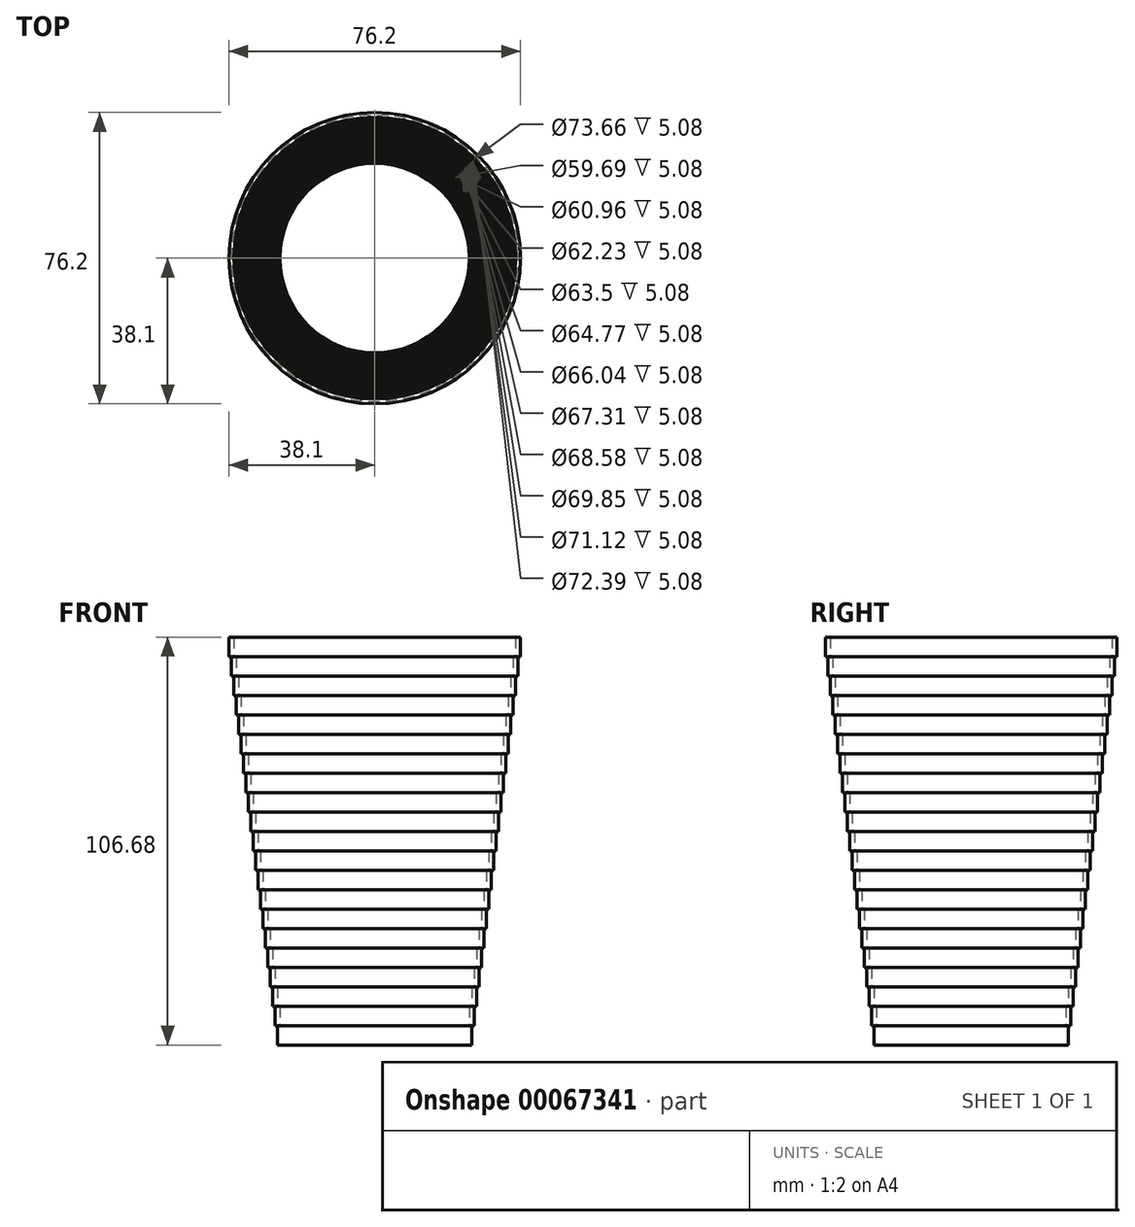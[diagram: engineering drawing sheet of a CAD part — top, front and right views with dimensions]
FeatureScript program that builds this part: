
annotation { "Feature Type Name" : "Feature", "Feature Type Description" : "" }
export const myFeature = defineFeature(function(context is Context, id is Id, definition is map)
    precondition{}
    {
        {
            var Q0;
            Q0=qCreatedBy(makeId("Top.planeOp"),FACE);
            var sketch = newSketch(context, id + "F0", { "sketchPlane" : qUnion([Q0])});
            skCircle(sketch, "E0", {"center": v(0, 0) * mm, "radius": 25.4 * mm});
            skSolve(sketch);
        }
        {
            var Q0;
            Q0=makeQuery(id+"F0.imprint","IMPRINT",FACE,{"disambiguationData":[TD([[makeQuery(id+"F0.imprint","IMPRINT",EDGE,{"derivedFrom":sQuery(id+"F0.wireOp",EDGE,"E0")}),1.0]])]});
            extrude(context, id + "F1", {"entities" : qUnion([Q0]), "depth" : 5.08 * mm});
        }
        {
            var Q0;
            Q0=makeQuery(id+"F1.opExtrude","CAP_FACE",FACE,{"disambiguationData":[OSD([sQuery(id+"F0.wireOp",EDGE,"E0")])],"isStart":false});
            var sketch = newSketch(context, id + "F2", { "sketchPlane" : qUnion([Q0])});
            skCircle(sketch, "E1", {"center": v(0, 0) * mm, "radius": 26.04 * mm});
            skCircle(sketch, "E2", {"center": v(0, 0) * mm, "radius": 24.77 * mm});
            skSolve(sketch);
        }
        {
            var Q0;
            Q0=makeQuery(id+"F2.imprint","IMPRINT",FACE,{"disambiguationData":[TD([[makeQuery(id+"F2.imprint","IMPRINT",EDGE,{"derivedFrom":sQuery(id+"F2.wireOp",EDGE,"E1")}),1.0]])]});
            var Q1;
            Q1=makeQuery(id+"F2.imprint","IMPRINT",FACE,{"disambiguationData":[TD([[makeQuery(id+"F2.imprint","IMPRINT",EDGE,{"derivedFrom":sQuery(id+"F2.wireOp",EDGE,"E2")}),-1.0]])]});
            extrude(context, id + "F3", {"entities" : qUnion([Q0, Q1]), "operationType" : NewBodyOperationType.ADD, "depth" : 5.08 * mm});
        }
        {
            var Q0;
            Q0=makeQuery(id+"F3.opExtrude","CAP_FACE",FACE,{"disambiguationData":[OSD([sQuery(id+"F2.wireOp",EDGE,"E1"),sQuery(id+"F2.wireOp",EDGE,"E2")])],"isStart":false});
            var sketch = newSketch(context, id + "F4", { "sketchPlane" : qUnion([Q0])});
            skCircle(sketch, "E3", {"center": v(0, 0) * mm, "radius": 26.67 * mm});
            skCircle(sketch, "E4", {"center": v(0, 0) * mm, "radius": 25.4 * mm});
            skSolve(sketch);
        }
        {
            var Q0;
            Q0=makeQuery(id+"F4.imprint","IMPRINT",FACE,{"disambiguationData":[TD([[makeQuery(id+"F4.imprint","IMPRINT",EDGE,{"derivedFrom":sQuery(id+"F4.wireOp",EDGE,"E4")}),-1.0]])]});
            var Q1;
            Q1=makeQuery(id+"F4.imprint","IMPRINT",FACE,{"disambiguationData":[TD([[makeQuery(id+"F4.imprint","IMPRINT",EDGE,{"derivedFrom":sQuery(id+"F4.wireOp",EDGE,"E3")}),1.0]])]});
            extrude(context, id + "F5", {"entities" : qUnion([Q0, Q1]), "operationType" : NewBodyOperationType.ADD, "depth" : 5.08 * mm});
        }
        {
            var Q0;
            Q0=makeQuery(id+"F5.opExtrude","CAP_FACE",FACE,{"disambiguationData":[OSD([sQuery(id+"F4.wireOp",EDGE,"E3"),sQuery(id+"F4.wireOp",EDGE,"E4")])],"isStart":false});
            var sketch = newSketch(context, id + "F6", { "sketchPlane" : qUnion([Q0])});
            skCircle(sketch, "E5", {"center": v(0, 0) * mm, "radius": 27.3 * mm});
            skCircle(sketch, "E6", {"center": v(0, 0) * mm, "radius": 26.04 * mm});
            skSolve(sketch);
        }
        {
            var Q0;
            Q0=makeQuery(id+"F6.imprint","IMPRINT",FACE,{"disambiguationData":[TD([[makeQuery(id+"F6.imprint","IMPRINT",EDGE,{"derivedFrom":sQuery(id+"F6.wireOp",EDGE,"E5")}),1.0]])]});
            var Q1;
            Q1=makeQuery(id+"F6.imprint","IMPRINT",FACE,{"disambiguationData":[TD([[makeQuery(id+"F6.imprint","IMPRINT",EDGE,{"derivedFrom":sQuery(id+"F6.wireOp",EDGE,"E6")}),-1.0]])]});
            extrude(context, id + "F7", {"entities" : qUnion([Q0, Q1]), "operationType" : NewBodyOperationType.ADD, "depth" : 5.08 * mm});
        }
        {
            var Q0;
            Q0=makeQuery(id+"F7.opExtrude","CAP_FACE",FACE,{"disambiguationData":[OSD([sQuery(id+"F6.wireOp",EDGE,"E5"),sQuery(id+"F6.wireOp",EDGE,"E6")])],"isStart":false});
            var sketch = newSketch(context, id + "F8", { "sketchPlane" : qUnion([Q0])});
            skCircle(sketch, "E7", {"center": v(0, 0) * mm, "radius": 27.94 * mm});
            skCircle(sketch, "E8", {"center": v(0, 0) * mm, "radius": 26.67 * mm});
            skSolve(sketch);
        }
        {
            var Q0;
            Q0=makeQuery(id+"F8.imprint","IMPRINT",FACE,{"disambiguationData":[TD([[makeQuery(id+"F8.imprint","IMPRINT",EDGE,{"derivedFrom":sQuery(id+"F8.wireOp",EDGE,"E8")}),-1.0]])]});
            var Q1;
            Q1=makeQuery(id+"F8.imprint","IMPRINT",FACE,{"disambiguationData":[TD([[makeQuery(id+"F8.imprint","IMPRINT",EDGE,{"derivedFrom":sQuery(id+"F8.wireOp",EDGE,"E7")}),1.0]])]});
            extrude(context, id + "F9", {"entities" : qUnion([Q0, Q1]), "operationType" : NewBodyOperationType.ADD, "depth" : 5.08 * mm});
        }
        {
            var Q0;
            Q0=makeQuery(id+"F9.opExtrude","CAP_FACE",FACE,{"disambiguationData":[OSD([sQuery(id+"F8.wireOp",EDGE,"E7"),sQuery(id+"F8.wireOp",EDGE,"E8")])],"isStart":false});
            var sketch = newSketch(context, id + "F10", { "sketchPlane" : qUnion([Q0])});
            skCircle(sketch, "E9", {"center": v(0, 0) * mm, "radius": 28.58 * mm});
            skCircle(sketch, "E10", {"center": v(0, 0) * mm, "radius": 27.3 * mm});
            skSolve(sketch);
        }
        {
            var Q0;
            Q0=makeQuery(id+"F10.imprint","IMPRINT",FACE,{"disambiguationData":[TD([[makeQuery(id+"F10.imprint","IMPRINT",EDGE,{"derivedFrom":sQuery(id+"F10.wireOp",EDGE,"E9")}),1.0]])]});
            var Q1;
            Q1=makeQuery(id+"F10.imprint","IMPRINT",FACE,{"disambiguationData":[TD([[makeQuery(id+"F10.imprint","IMPRINT",EDGE,{"derivedFrom":sQuery(id+"F10.wireOp",EDGE,"E10")}),-1.0]])]});
            extrude(context, id + "F11", {"entities" : qUnion([Q0, Q1]), "operationType" : NewBodyOperationType.ADD, "depth" : 5.08 * mm});
        }
        {
            var Q0;
            Q0=makeQuery(id+"F11.opExtrude","CAP_FACE",FACE,{"disambiguationData":[OSD([sQuery(id+"F10.wireOp",EDGE,"E9"),sQuery(id+"F10.wireOp",EDGE,"E10")])],"isStart":false});
            var sketch = newSketch(context, id + "F12", { "sketchPlane" : qUnion([Q0])});
            skCircle(sketch, "E11", {"center": v(0, 0) * mm, "radius": 29.21 * mm});
            skCircle(sketch, "E12", {"center": v(0, 0) * mm, "radius": 27.94 * mm});
            skSolve(sketch);
        }
        {
            var Q0;
            Q0=makeQuery(id+"F12.imprint","IMPRINT",FACE,{"disambiguationData":[TD([[makeQuery(id+"F12.imprint","IMPRINT",EDGE,{"derivedFrom":sQuery(id+"F12.wireOp",EDGE,"E12")}),-1.0]])]});
            var Q1;
            Q1=makeQuery(id+"F12.imprint","IMPRINT",FACE,{"disambiguationData":[TD([[makeQuery(id+"F12.imprint","IMPRINT",EDGE,{"derivedFrom":sQuery(id+"F12.wireOp",EDGE,"E11")}),1.0]])]});
            extrude(context, id + "F13", {"entities" : qUnion([Q0, Q1]), "operationType" : NewBodyOperationType.ADD, "depth" : 5.08 * mm});
        }
        {
            var Q0;
            Q0=makeQuery(id+"F13.opExtrude","CAP_FACE",FACE,{"disambiguationData":[OSD([sQuery(id+"F12.wireOp",EDGE,"E11"),sQuery(id+"F12.wireOp",EDGE,"E12")])],"isStart":false});
            var sketch = newSketch(context, id + "F14", { "sketchPlane" : qUnion([Q0])});
            skCircle(sketch, "E13", {"center": v(0, 0) * mm, "radius": 29.85 * mm});
            skCircle(sketch, "E14", {"center": v(0, 0) * mm, "radius": 28.58 * mm});
            skSolve(sketch);
        }
        {
            var Q0;
            Q0=makeQuery(id+"F14.imprint","IMPRINT",FACE,{"disambiguationData":[TD([[makeQuery(id+"F14.imprint","IMPRINT",EDGE,{"derivedFrom":sQuery(id+"F14.wireOp",EDGE,"E13")}),1.0]])]});
            var Q1;
            Q1=makeQuery(id+"F14.imprint","IMPRINT",FACE,{"disambiguationData":[TD([[makeQuery(id+"F14.imprint","IMPRINT",EDGE,{"derivedFrom":sQuery(id+"F14.wireOp",EDGE,"E14")}),-1.0]])]});
            extrude(context, id + "F15", {"entities" : qUnion([Q0, Q1]), "operationType" : NewBodyOperationType.ADD, "depth" : 5.08 * mm});
        }
        {
            var Q0;
            Q0=makeQuery(id+"F15.opExtrude","CAP_FACE",FACE,{"disambiguationData":[OSD([sQuery(id+"F14.wireOp",EDGE,"E13"),sQuery(id+"F14.wireOp",EDGE,"E14")])],"isStart":false});
            var sketch = newSketch(context, id + "F16", { "sketchPlane" : qUnion([Q0])});
            skCircle(sketch, "E15", {"center": v(0, 0) * mm, "radius": 30.48 * mm});
            skCircle(sketch, "E16", {"center": v(0, 0) * mm, "radius": 29.21 * mm});
            skSolve(sketch);
        }
        {
            var Q0;
            Q0=makeQuery(id+"F16.imprint","IMPRINT",FACE,{"disambiguationData":[TD([[makeQuery(id+"F16.imprint","IMPRINT",EDGE,{"derivedFrom":sQuery(id+"F16.wireOp",EDGE,"E15")}),1.0]])]});
            var Q1;
            Q1=makeQuery(id+"F16.imprint","IMPRINT",FACE,{"disambiguationData":[TD([[makeQuery(id+"F16.imprint","IMPRINT",EDGE,{"derivedFrom":sQuery(id+"F16.wireOp",EDGE,"E16")}),-1.0]])]});
            extrude(context, id + "F17", {"entities" : qUnion([Q0, Q1]), "operationType" : NewBodyOperationType.ADD, "depth" : 5.08 * mm});
        }
        {
            var Q0;
            Q0=makeQuery(id+"F17.opExtrude","CAP_FACE",FACE,{"disambiguationData":[OSD([sQuery(id+"F16.wireOp",EDGE,"E15"),sQuery(id+"F16.wireOp",EDGE,"E16")])],"isStart":false});
            var sketch = newSketch(context, id + "F18", { "sketchPlane" : qUnion([Q0])});
            skCircle(sketch, "E17", {"center": v(0, 0) * mm, "radius": 31.12 * mm});
            skCircle(sketch, "E18", {"center": v(0, 0) * mm, "radius": 29.85 * mm});
            skSolve(sketch);
        }
        {
            var Q0;
            Q0=makeQuery(id+"F18.imprint","IMPRINT",FACE,{"disambiguationData":[TD([[makeQuery(id+"F18.imprint","IMPRINT",EDGE,{"derivedFrom":sQuery(id+"F18.wireOp",EDGE,"E18")}),-1.0]])]});
            var Q1;
            Q1=makeQuery(id+"F18.imprint","IMPRINT",FACE,{"disambiguationData":[TD([[makeQuery(id+"F18.imprint","IMPRINT",EDGE,{"derivedFrom":sQuery(id+"F18.wireOp",EDGE,"E17")}),1.0]])]});
            extrude(context, id + "F19", {"entities" : qUnion([Q0, Q1]), "operationType" : NewBodyOperationType.ADD, "depth" : 5.08 * mm});
        }
        {
            var Q0;
            Q0=makeQuery(id+"F19.opExtrude","CAP_FACE",FACE,{"disambiguationData":[OSD([sQuery(id+"F18.wireOp",EDGE,"E17"),sQuery(id+"F18.wireOp",EDGE,"E18")])],"isStart":false});
            var sketch = newSketch(context, id + "F20", { "sketchPlane" : qUnion([Q0])});
            skCircle(sketch, "E19", {"center": v(0, 0) * mm, "radius": 31.75 * mm});
            skCircle(sketch, "E20", {"center": v(0, 0) * mm, "radius": 30.48 * mm});
            skSolve(sketch);
        }
        {
            var Q0;
            Q0=makeQuery(id+"F20.imprint","IMPRINT",FACE,{"disambiguationData":[TD([[makeQuery(id+"F20.imprint","IMPRINT",EDGE,{"derivedFrom":sQuery(id+"F20.wireOp",EDGE,"E19")}),1.0]])]});
            var Q1;
            Q1=makeQuery(id+"F20.imprint","IMPRINT",FACE,{"disambiguationData":[TD([[makeQuery(id+"F20.imprint","IMPRINT",EDGE,{"derivedFrom":sQuery(id+"F20.wireOp",EDGE,"E20")}),-1.0]])]});
            extrude(context, id + "F21", {"entities" : qUnion([Q0, Q1]), "operationType" : NewBodyOperationType.ADD, "depth" : 5.08 * mm});
        }
        {
            var Q0;
            Q0=makeQuery(id+"F21.opExtrude","CAP_FACE",FACE,{"disambiguationData":[OSD([sQuery(id+"F20.wireOp",EDGE,"E19"),sQuery(id+"F20.wireOp",EDGE,"E20")])],"isStart":false});
            var sketch = newSketch(context, id + "F22", { "sketchPlane" : qUnion([Q0])});
            skCircle(sketch, "E21", {"center": v(0, 0) * mm, "radius": 32.39 * mm});
            skCircle(sketch, "E22", {"center": v(0, 0) * mm, "radius": 31.12 * mm});
            skSolve(sketch);
        }
        {
            var Q0;
            Q0=makeQuery(id+"F22.imprint","IMPRINT",FACE,{"disambiguationData":[TD([[makeQuery(id+"F22.imprint","IMPRINT",EDGE,{"derivedFrom":sQuery(id+"F22.wireOp",EDGE,"E21")}),1.0]])]});
            var Q1;
            Q1=makeQuery(id+"F22.imprint","IMPRINT",FACE,{"disambiguationData":[TD([[makeQuery(id+"F22.imprint","IMPRINT",EDGE,{"derivedFrom":sQuery(id+"F22.wireOp",EDGE,"E22")}),-1.0]])]});
            extrude(context, id + "F23", {"entities" : qUnion([Q0, Q1]), "operationType" : NewBodyOperationType.ADD, "depth" : 5.08 * mm});
        }
        {
            var Q0;
            Q0=makeQuery(id+"F23.opExtrude","CAP_FACE",FACE,{"disambiguationData":[OSD([sQuery(id+"F22.wireOp",EDGE,"E21"),sQuery(id+"F22.wireOp",EDGE,"E22")])],"isStart":false});
            var sketch = newSketch(context, id + "F24", { "sketchPlane" : qUnion([Q0])});
            skCircle(sketch, "E23", {"center": v(0, 0) * mm, "radius": 33.02 * mm});
            skCircle(sketch, "E24", {"center": v(0, 0) * mm, "radius": 31.75 * mm});
            skSolve(sketch);
        }
        {
            var Q0;
            Q0=makeQuery(id+"F24.imprint","IMPRINT",FACE,{"disambiguationData":[TD([[makeQuery(id+"F24.imprint","IMPRINT",EDGE,{"derivedFrom":sQuery(id+"F24.wireOp",EDGE,"E23")}),1.0]])]});
            var Q1;
            Q1=makeQuery(id+"F24.imprint","IMPRINT",FACE,{"disambiguationData":[TD([[makeQuery(id+"F24.imprint","IMPRINT",EDGE,{"derivedFrom":sQuery(id+"F24.wireOp",EDGE,"E24")}),-1.0]])]});
            extrude(context, id + "F25", {"entities" : qUnion([Q0, Q1]), "operationType" : NewBodyOperationType.ADD, "depth" : 5.08 * mm});
        }
        {
            var Q0;
            Q0=makeQuery(id+"F25.opExtrude","CAP_FACE",FACE,{"disambiguationData":[OSD([sQuery(id+"F24.wireOp",EDGE,"E23"),sQuery(id+"F24.wireOp",EDGE,"E24")])],"isStart":false});
            var sketch = newSketch(context, id + "F26", { "sketchPlane" : qUnion([Q0])});
            skCircle(sketch, "E25", {"center": v(0, 0) * mm, "radius": 33.66 * mm});
            skCircle(sketch, "E26", {"center": v(0, 0) * mm, "radius": 32.39 * mm});
            skSolve(sketch);
        }
        {
            var Q0;
            Q0=makeQuery(id+"F26.imprint","IMPRINT",FACE,{"disambiguationData":[TD([[makeQuery(id+"F26.imprint","IMPRINT",EDGE,{"derivedFrom":sQuery(id+"F26.wireOp",EDGE,"E26")}),-1.0]])]});
            var Q1;
            Q1=makeQuery(id+"F26.imprint","IMPRINT",FACE,{"disambiguationData":[TD([[makeQuery(id+"F26.imprint","IMPRINT",EDGE,{"derivedFrom":sQuery(id+"F26.wireOp",EDGE,"E25")}),1.0]])]});
            extrude(context, id + "F27", {"entities" : qUnion([Q0, Q1]), "operationType" : NewBodyOperationType.ADD, "depth" : 5.08 * mm});
        }
        {
            var Q0;
            Q0=makeQuery(id+"F27.opExtrude","CAP_FACE",FACE,{"disambiguationData":[OSD([sQuery(id+"F26.wireOp",EDGE,"E25"),sQuery(id+"F26.wireOp",EDGE,"E26")])],"isStart":false});
            var sketch = newSketch(context, id + "F28", { "sketchPlane" : qUnion([Q0])});
            skCircle(sketch, "E27", {"center": v(0, 0) * mm, "radius": 34.3 * mm});
            skCircle(sketch, "E28", {"center": v(0, 0) * mm, "radius": 33.02 * mm});
            skSolve(sketch);
        }
        {
            var Q0;
            Q0=makeQuery(id+"F28.imprint","IMPRINT",FACE,{"disambiguationData":[TD([[makeQuery(id+"F28.imprint","IMPRINT",EDGE,{"derivedFrom":sQuery(id+"F28.wireOp",EDGE,"E27")}),1.0]])]});
            var Q1;
            Q1=makeQuery(id+"F28.imprint","IMPRINT",FACE,{"disambiguationData":[TD([[makeQuery(id+"F28.imprint","IMPRINT",EDGE,{"derivedFrom":sQuery(id+"F28.wireOp",EDGE,"E28")}),-1.0]])]});
            extrude(context, id + "F29", {"entities" : qUnion([Q0, Q1]), "operationType" : NewBodyOperationType.ADD, "depth" : 5.08 * mm});
        }
        {
            var Q0;
            Q0=makeQuery(id+"F29.opExtrude","CAP_FACE",FACE,{"disambiguationData":[OSD([sQuery(id+"F28.wireOp",EDGE,"E27"),sQuery(id+"F28.wireOp",EDGE,"E28")])],"isStart":false});
            var sketch = newSketch(context, id + "F30", { "sketchPlane" : qUnion([Q0])});
            skCircle(sketch, "E29", {"center": v(0, 0) * mm, "radius": 34.93 * mm});
            skCircle(sketch, "E30", {"center": v(0, 0) * mm, "radius": 33.66 * mm});
            skSolve(sketch);
        }
        {
            var Q0;
            Q0=makeQuery(id+"F30.imprint","IMPRINT",FACE,{"disambiguationData":[TD([[makeQuery(id+"F30.imprint","IMPRINT",EDGE,{"derivedFrom":sQuery(id+"F30.wireOp",EDGE,"E30")}),-1.0]])]});
            var Q1;
            Q1=makeQuery(id+"F30.imprint","IMPRINT",FACE,{"disambiguationData":[TD([[makeQuery(id+"F30.imprint","IMPRINT",EDGE,{"derivedFrom":sQuery(id+"F30.wireOp",EDGE,"E29")}),1.0]])]});
            extrude(context, id + "F31", {"entities" : qUnion([Q0, Q1]), "operationType" : NewBodyOperationType.ADD, "depth" : 5.08 * mm});
        }
        {
            var Q0;
            Q0=makeQuery(id+"F31.opExtrude","CAP_FACE",FACE,{"disambiguationData":[OSD([sQuery(id+"F30.wireOp",EDGE,"E29"),sQuery(id+"F30.wireOp",EDGE,"E30")])],"isStart":false});
            var sketch = newSketch(context, id + "F32", { "sketchPlane" : qUnion([Q0])});
            skCircle(sketch, "E31", {"center": v(0, 0) * mm, "radius": 35.56 * mm});
            skCircle(sketch, "E32", {"center": v(0, 0) * mm, "radius": 34.3 * mm});
            skSolve(sketch);
        }
        {
            var Q0;
            Q0=makeQuery(id+"F32.imprint","IMPRINT",FACE,{"disambiguationData":[TD([[makeQuery(id+"F32.imprint","IMPRINT",EDGE,{"derivedFrom":sQuery(id+"F32.wireOp",EDGE,"E32")}),-1.0]])]});
            var Q1;
            Q1=makeQuery(id+"F32.imprint","IMPRINT",FACE,{"disambiguationData":[TD([[makeQuery(id+"F32.imprint","IMPRINT",EDGE,{"derivedFrom":sQuery(id+"F32.wireOp",EDGE,"E31")}),1.0]])]});
            extrude(context, id + "F33", {"entities" : qUnion([Q0, Q1]), "operationType" : NewBodyOperationType.ADD, "depth" : 5.08 * mm});
        }
        {
            var Q0;
            Q0=makeQuery(id+"F33.opExtrude","CAP_FACE",FACE,{"disambiguationData":[OSD([sQuery(id+"F32.wireOp",EDGE,"E31"),sQuery(id+"F32.wireOp",EDGE,"E32")])],"isStart":false});
            var sketch = newSketch(context, id + "F34", { "sketchPlane" : qUnion([Q0])});
            skCircle(sketch, "E33", {"center": v(0, 0) * mm, "radius": 34.93 * mm});
            skCircle(sketch, "E34", {"center": v(0, 0) * mm, "radius": 36.2 * mm});
            skSolve(sketch);
        }
        {
            var Q0;
            Q0=makeQuery(id+"F34.imprint","IMPRINT",FACE,{"disambiguationData":[TD([[makeQuery(id+"F34.imprint","IMPRINT",EDGE,{"derivedFrom":sQuery(id+"F34.wireOp",EDGE,"E33")}),-1.0]])]});
            var Q1;
            Q1=makeQuery(id+"F34.imprint","IMPRINT",FACE,{"disambiguationData":[TD([[makeQuery(id+"F34.imprint","IMPRINT",EDGE,{"derivedFrom":sQuery(id+"F34.wireOp",EDGE,"E34")}),1.0]])]});
            extrude(context, id + "F35", {"entities" : qUnion([Q0, Q1]), "operationType" : NewBodyOperationType.ADD, "depth" : 5.08 * mm});
        }
        {
            var Q0;
            Q0=makeQuery(id+"F35.opExtrude","CAP_FACE",FACE,{"disambiguationData":[OSD([sQuery(id+"F34.wireOp",EDGE,"E33"),sQuery(id+"F34.wireOp",EDGE,"E34")])],"isStart":false});
            var sketch = newSketch(context, id + "F36", { "sketchPlane" : qUnion([Q0])});
            skCircle(sketch, "E35", {"center": v(0, 0) * mm, "radius": 36.83 * mm});
            skCircle(sketch, "E36", {"center": v(0, 0) * mm, "radius": 35.56 * mm});
            skSolve(sketch);
        }
        {
            var Q0;
            Q0=makeQuery(id+"F36.imprint","IMPRINT",FACE,{"disambiguationData":[TD([[makeQuery(id+"F36.imprint","IMPRINT",EDGE,{"derivedFrom":sQuery(id+"F36.wireOp",EDGE,"E36")}),-1.0]])]});
            var Q1;
            Q1=makeQuery(id+"F36.imprint","IMPRINT",FACE,{"disambiguationData":[TD([[makeQuery(id+"F36.imprint","IMPRINT",EDGE,{"derivedFrom":sQuery(id+"F36.wireOp",EDGE,"E35")}),1.0]])]});
            extrude(context, id + "F37", {"entities" : qUnion([Q0, Q1]), "operationType" : NewBodyOperationType.ADD, "depth" : 5.08 * mm});
        }
        {
            var Q0;
            Q0=makeQuery(id+"F37.opExtrude","CAP_FACE",FACE,{"disambiguationData":[OSD([sQuery(id+"F36.wireOp",EDGE,"E35"),sQuery(id+"F36.wireOp",EDGE,"E36")])],"isStart":false});
            var sketch = newSketch(context, id + "F38", { "sketchPlane" : qUnion([Q0])});
            skCircle(sketch, "E37", {"center": v(0, 0) * mm, "radius": 37.47 * mm});
            skCircle(sketch, "E38", {"center": v(0, 0) * mm, "radius": 36.2 * mm});
            skSolve(sketch);
        }
        {
            var Q0;
            Q0=makeQuery(id+"F38.imprint","IMPRINT",FACE,{"disambiguationData":[TD([[makeQuery(id+"F38.imprint","IMPRINT",EDGE,{"derivedFrom":sQuery(id+"F38.wireOp",EDGE,"E38")}),-1.0]])]});
            var Q1;
            Q1=makeQuery(id+"F38.imprint","IMPRINT",FACE,{"disambiguationData":[TD([[makeQuery(id+"F38.imprint","IMPRINT",EDGE,{"derivedFrom":sQuery(id+"F38.wireOp",EDGE,"E37")}),1.0]])]});
            extrude(context, id + "F39", {"entities" : qUnion([Q0, Q1]), "operationType" : NewBodyOperationType.ADD, "depth" : 5.08 * mm});
        }
        {
            var Q0;
            Q0=makeQuery(id+"F39.opExtrude","CAP_FACE",FACE,{"disambiguationData":[OSD([sQuery(id+"F38.wireOp",EDGE,"E37"),sQuery(id+"F38.wireOp",EDGE,"E38")])],"isStart":false});
            var sketch = newSketch(context, id + "F40", { "sketchPlane" : qUnion([Q0])});
            skCircle(sketch, "E39", {"center": v(0, 0) * mm, "radius": 38.1 * mm});
            skCircle(sketch, "E40", {"center": v(0, 0) * mm, "radius": 36.83 * mm});
            skSolve(sketch);
        }
        {
            var Q0;
            Q0=makeQuery(id+"F40.imprint","IMPRINT",FACE,{"disambiguationData":[TD([[makeQuery(id+"F40.imprint","IMPRINT",EDGE,{"derivedFrom":sQuery(id+"F40.wireOp",EDGE,"E39")}),1.0]])]});
            var Q1;
            Q1=makeQuery(id+"F40.imprint","IMPRINT",FACE,{"disambiguationData":[TD([[makeQuery(id+"F40.imprint","IMPRINT",EDGE,{"derivedFrom":sQuery(id+"F40.wireOp",EDGE,"E40")}),-1.0]])]});
            extrude(context, id + "F41", {"entities" : qUnion([Q0, Q1]), "operationType" : NewBodyOperationType.ADD, "depth" : 5.08 * mm});
        }
    });
